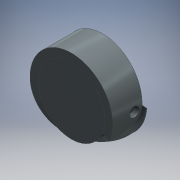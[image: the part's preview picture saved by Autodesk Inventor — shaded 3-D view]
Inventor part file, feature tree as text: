
AUTODESK INVENTOR PART (.ipt)
format: ipt  version: 2016 (Build 200138000, 138)  size: 365,056 bytes
history: native  units: mm
features: sketch x10, other x5, extrude x5, plane x2, fillet x2, hole x2, projected_geometry x2, surface_op x1, reference x1, loft x1
ambient origin geometry x8: Origin, YZ Plane, XZ Plane, XY Plane, X Axis, Y Axis, Z Axis, Center Point
bodies: Solid1 (feature_tree)
feature tree (31):
  other  "Fixture.ipt"
  extrude  "Extrusion1"  TaperAngle=0.0deg  [1 undecoded]
  plane  "Work Plane4"
  sketch  "Sketch4"  dims[d15=5.3mm d16=21.0mm]
  sketch  "3D Sketch5"
  sketch  "3D Sketch6"
  surface_op  "Sculpt3"
  extrude  "Extrusion2"  Depth=21.0mm
  extrude  "Extrusion3"  Depth=1.9mm TaperAngle=0.0deg
  extrude  "Extrusion4"  TaperAngle=0.0deg  [1 undecoded]
  fillet  "Fillet5"  Radius=4.65mm
  plane  "Work Plane5"
  sketch  "Sketch15"  dims[d77=159.907066mm d79=1.047198mm d81=1.047198mm d82=10.0mm d83=21.0mm d84=0.0mm d85=90.0deg d86=0.0mm d87=90.0deg d88=17.9mm d89=0.1mm d90=3.1mm d91=6.0mm d92=4.0mm d93=2.0mm d94=90.0deg d95=8.0mm d96=20.594885mm d97=6.0mm d98=6.0mm d99=4.0mm d100=2.0mm d101=90.0deg d102=3.449977mm d103=20.594885mm]
  hole  "Hole5"  [1 undecoded]
  sketch  "3D Sketch7"
  hole  "Hole6"  [1 undecoded]
  fillet  "Fillet2"  Radius=5.0mm
  sketch  "Sketch1"  dims[d2=21.0mm d3=0.0mm]
  other  "Srf1"
  sketch  "Sketch5"  dims[d17=0.0mm d24=1.9mm d25=0.0mm]
  sketch  "Sketch7"  dims[d40=6.1mm d41=0.0mm d57=4.65mm]
  sketch  "Sketch9"  dims[d58=14.55mm d59=0.0mm d60=3.0mm]
  sketch  "Sketch12"  dims[d74=10.0mm d75=50.9mm d76=5.0mm]
  projected_geometry  "Projected Loop3"
  other  "Project to Surface6"
  other  "Project to Surface7"
  other  "Srf4"
  projected_geometry  "Projected Loop4"
  reference  "Reference6"
  extrude  "ExtrusionSrf1"  Depth=10.0mm
  loft  "LoftSrf3"
note: 4 required parameter values undecoded (feature->parameter linkage not recoverable at this tier; creation-order binding heuristic only, values carry confidence <= 0.55)
